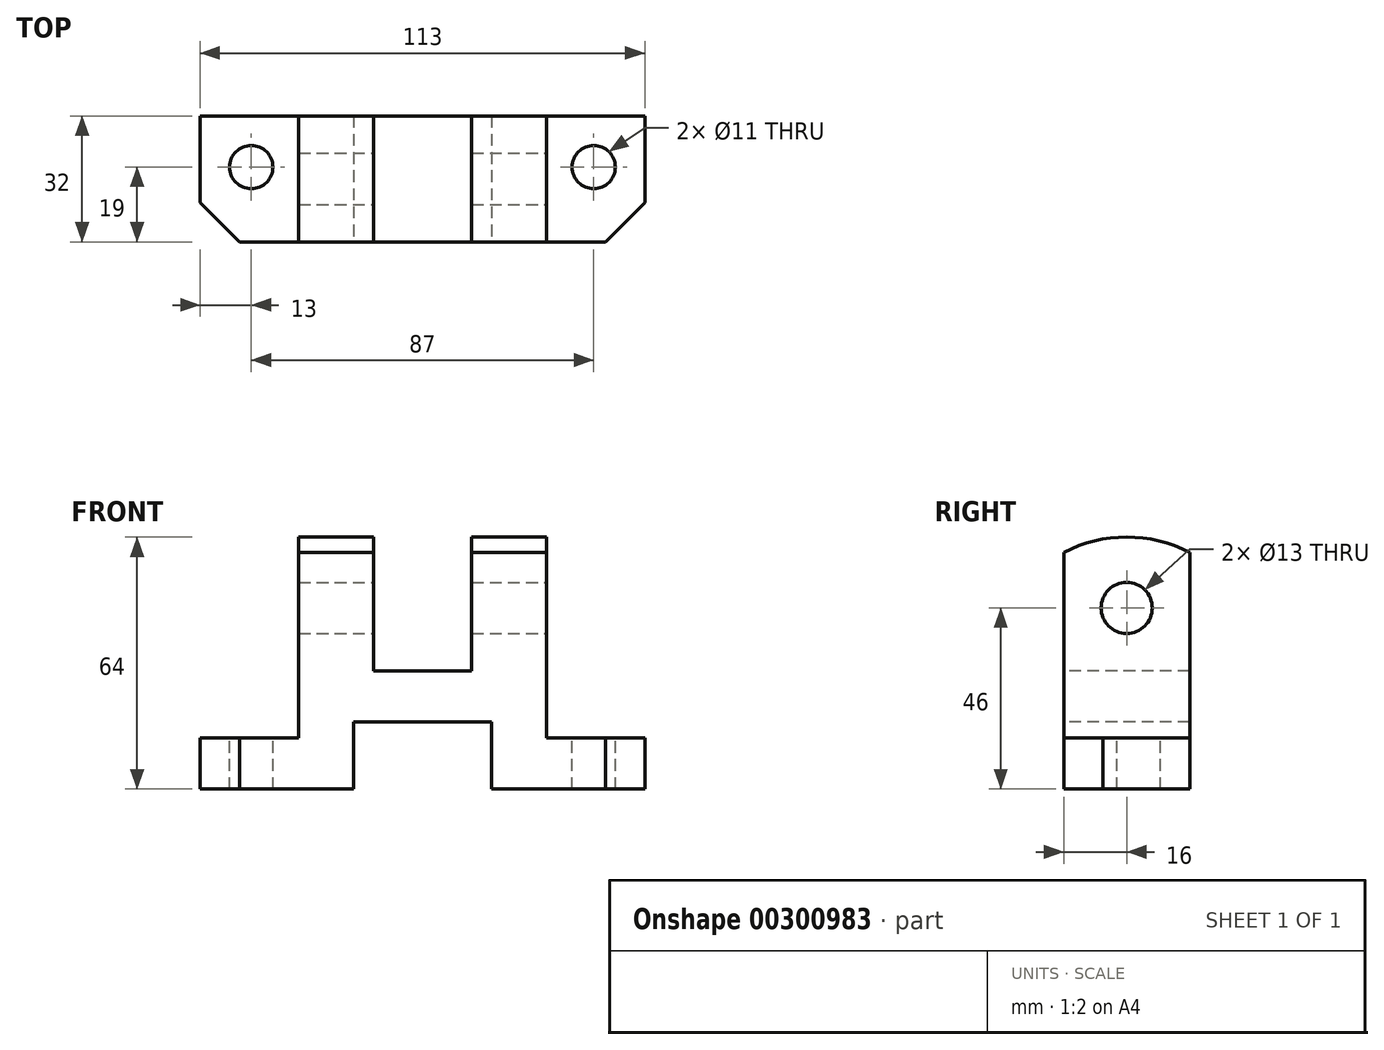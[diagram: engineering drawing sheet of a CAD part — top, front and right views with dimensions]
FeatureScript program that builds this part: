
annotation { "Feature Type Name" : "Feature", "Feature Type Description" : "" }
export const myFeature = defineFeature(function(context is Context, id is Id, definition is map)
    precondition{}
    {
        {
            var Q0;
            Q0=qCreatedBy(makeId("Front.planeOp"),FACE);
            var sketch = newSketch(context, id + "F0", { "sketchPlane" : qUnion([Q0])});
            skLineSegment(sketch, "E0", {"start": v(25, 60.13) * mm, "end": v(44, 60.13) * mm});
            skLineSegment(sketch, "E1", {"start": v(44, 60.13) * mm, "end": v(44, 30) * mm});
            skLineSegment(sketch, "E2", {"start": v(69, 30) * mm, "end": v(69, 60.13) * mm});
            skLineSegment(sketch, "E3", {"start": v(69, 60.13) * mm, "end": v(88, 60.13) * mm});
            skLineSegment(sketch, "E4", {"start": v(113, 13) * mm, "end": v(113, 0) * mm});
            skLineSegment(sketch, "E5", {"start": v(0, 0) * mm, "end": v(39, 0) * mm});
            skLineSegment(sketch, "E6", {"start": v(39, 0) * mm, "end": v(39, 17) * mm});
            skLineSegment(sketch, "E7", {"start": v(39, 17) * mm, "end": v(74, 17) * mm});
            skLineSegment(sketch, "E8", {"start": v(74, 17) * mm, "end": v(74, 0) * mm});
            skLineSegment(sketch, "E9", {"start": v(74, 0) * mm, "end": v(113, 0) * mm});
            skLineSegment(sketch, "E10", {"start": v(0, 0) * mm, "end": v(0, 13) * mm});
            skLineSegment(sketch, "E11", {"start": v(113, 13) * mm, "end": v(88, 13) * mm});
            skLineSegment(sketch, "E12", {"start": v(88, 13) * mm, "end": v(88, 60.13) * mm});
            skLineSegment(sketch, "E13", {"start": v(0, 13) * mm, "end": v(25, 13) * mm});
            skLineSegment(sketch, "E14", {"start": v(25, 13) * mm, "end": v(25, 60.13) * mm});
            skLineSegment(sketch, "E15", {"start": v(44, 30) * mm, "end": v(69, 30) * mm});
            skSolve(sketch);
        }
        {
            var Q0;
            Q0=makeQuery(id+"F0.imprint","IMPRINT",FACE,{"disambiguationData":[TD([[makeQuery(id+"F0.imprint","IMPRINT",EDGE,{"derivedFrom":sQuery(id+"F0.wireOp",EDGE,"E0")}),-1.0]])]});
            extrude(context, id + "F1", {"entities" : qUnion([Q0]), "oppositeDirection" : true, "depth" : 32 * mm});
        }
        {
            var Q0;
            Q0=makeQuery(id+"F1.opExtrude","SWEPT_FACE",FACE,{"disambiguationData":[OSD([sQuery(id+"F0.wireOp",EDGE,"E11")])]});
            var sketch = newSketch(context, id + "F2", { "sketchPlane" : qUnion([Q0])});
            skCircle(sketch, "E16", {"center": v(100, 19) * mm, "radius": 5.5 * mm});
            skLineSegment(sketch, "E17", {"start": v(103, 0) * mm, "end": v(113, 10) * mm});
            skSolve(sketch);
        }
        {
            var Q0;
            Q0=makeQuery(id+"F1.opExtrude","SWEPT_FACE",FACE,{"disambiguationData":[OSD([sQuery(id+"F0.wireOp",EDGE,"E12")])]});
            var sketch = newSketch(context, id + "F3", { "sketchPlane" : qUnion([Q0])});
            skCircle(sketch, "E18", {"center": v(16, 46) * mm, "radius": 6.5 * mm});
            skArc(sketch, "E19", {"start": v(32, 60.13) * mm, "mid": v(16, 64) * mm, "end": v(0, 60.13) * mm});
            skSolve(sketch);
        }
        {
            var Q0;
            Q0=makeQuery(id+"F1.opExtrude","SWEPT_FACE",FACE,{"disambiguationData":[OSD([sQuery(id+"F0.wireOp",EDGE,"E1")])]});
            var sketch = newSketch(context, id + "F4", { "sketchPlane" : qUnion([Q0])});
            skCircle(sketch, "E20", {"center": v(16, 46) * mm, "radius": 6.5 * mm});
            skArc(sketch, "E21", {"start": v(32, 60.13) * mm, "mid": v(16, 64) * mm, "end": v(0, 60.13) * mm});
            skSolve(sketch);
        }
        {
            var Q0;
            Q0=makeQuery(id+"F1.opExtrude","SWEPT_FACE",FACE,{"disambiguationData":[OSD([sQuery(id+"F0.wireOp",EDGE,"E13")])]});
            var sketch = newSketch(context, id + "F5", { "sketchPlane" : qUnion([Q0])});
            skCircle(sketch, "E22", {"center": v(13, 19) * mm, "radius": 5.5 * mm});
            skLineSegment(sketch, "E23", {"start": v(0, 10) * mm, "end": v(10, 0) * mm});
            skSolve(sketch);
        }
        {
            var Q0;
            Q0=makeQuery(id+"F2.imprint","IMPRINT",FACE,{"disambiguationData":[TD([[makeQuery(id+"F2.imprint","IMPRINT",EDGE,{"derivedFrom":sQuery(id+"F2.wireOp",EDGE,"E16")}),1.0]])]});
            extrude(context, id + "F6", {"entities" : qUnion([Q0]), "operationType" : NewBodyOperationType.REMOVE, "oppositeDirection" : true, "depth" : 25 * mm});
        }
        {
            var Q0;
            {var subQ0=sQuery(id+"F2.wireOp",EDGE,"E17");Q0=makeQuery(id+"F2.imprint","IMPRINT",FACE,{"disambiguationData":[TD([[makeQuery(id+"F2.imprint","IMPRINT",EDGE,{"derivedFrom":subQ0}),-1.0]])]});}
            extrude(context, id + "F7", {"entities" : qUnion([Q0]), "operationType" : NewBodyOperationType.REMOVE, "oppositeDirection" : true, "depth" : 25 * mm});
        }
        {
            var Q0;
            Q0=makeQuery(id+"F3.imprint","IMPRINT",FACE,{"disambiguationData":[TD([[makeQuery(id+"F3.imprint","IMPRINT",EDGE,{"derivedFrom":sQuery(id+"F3.wireOp",EDGE,"E18")}),1.0]])]});
            extrude(context, id + "F8", {"entities" : qUnion([Q0]), "operationType" : NewBodyOperationType.REMOVE, "oppositeDirection" : true, "depth" : 25 * mm});
        }
        {
            var Q0;
            Q0=makeQuery(id+"F4.imprint","IMPRINT",FACE,{"disambiguationData":[TD([[makeQuery(id+"F4.imprint","IMPRINT",EDGE,{"derivedFrom":sQuery(id+"F4.wireOp",EDGE,"E20")}),1.0]])]});
            extrude(context, id + "F9", {"entities" : qUnion([Q0]), "operationType" : NewBodyOperationType.REMOVE, "oppositeDirection" : true, "depth" : 25 * mm});
        }
        {
            var Q0;
            Q0=makeQuery(id+"F5.imprint","IMPRINT",FACE,{"disambiguationData":[TD([[makeQuery(id+"F5.imprint","IMPRINT",EDGE,{"derivedFrom":sQuery(id+"F5.wireOp",EDGE,"E22")}),1.0]])]});
            extrude(context, id + "F10", {"entities" : qUnion([Q0]), "operationType" : NewBodyOperationType.REMOVE, "oppositeDirection" : true, "depth" : 25 * mm});
        }
        {
            var Q0;
            {var subQ0=sQuery(id+"F5.wireOp",EDGE,"E23");Q0=makeQuery(id+"F5.imprint","IMPRINT",FACE,{"disambiguationData":[TD([[makeQuery(id+"F5.imprint","IMPRINT",EDGE,{"derivedFrom":subQ0}),-1.0]])]});}
            extrude(context, id + "F11", {"entities" : qUnion([Q0]), "operationType" : NewBodyOperationType.REMOVE, "oppositeDirection" : true, "depth" : 25 * mm});
        }
        {
            var Q0;
            Q0=makeQuery(id+"F3.imprint","IMPRINT",FACE,{"disambiguationData":[TD([[makeQuery(id+"F3.imprint","IMPRINT",EDGE,{"derivedFrom":sQuery(id+"F3.wireOp",EDGE,"E19")}),1.0]])]});
            extrude(context, id + "F12", {"entities" : qUnion([Q0]), "operationType" : NewBodyOperationType.ADD, "oppositeDirection" : true, "depth" : 63 * mm});
        }
        {
            var Q0;
            Q0=makeQuery(id+"F4.imprint","IMPRINT",FACE,{"disambiguationData":[TD([[makeQuery(id+"F4.imprint","IMPRINT",EDGE,{"derivedFrom":sQuery(id+"F4.wireOp",EDGE,"E21")}),1.0]])]});
            extrude(context, id + "F13", {"entities" : qUnion([Q0]), "operationType" : NewBodyOperationType.REMOVE, "depth" : 25 * mm});
        }
    });
